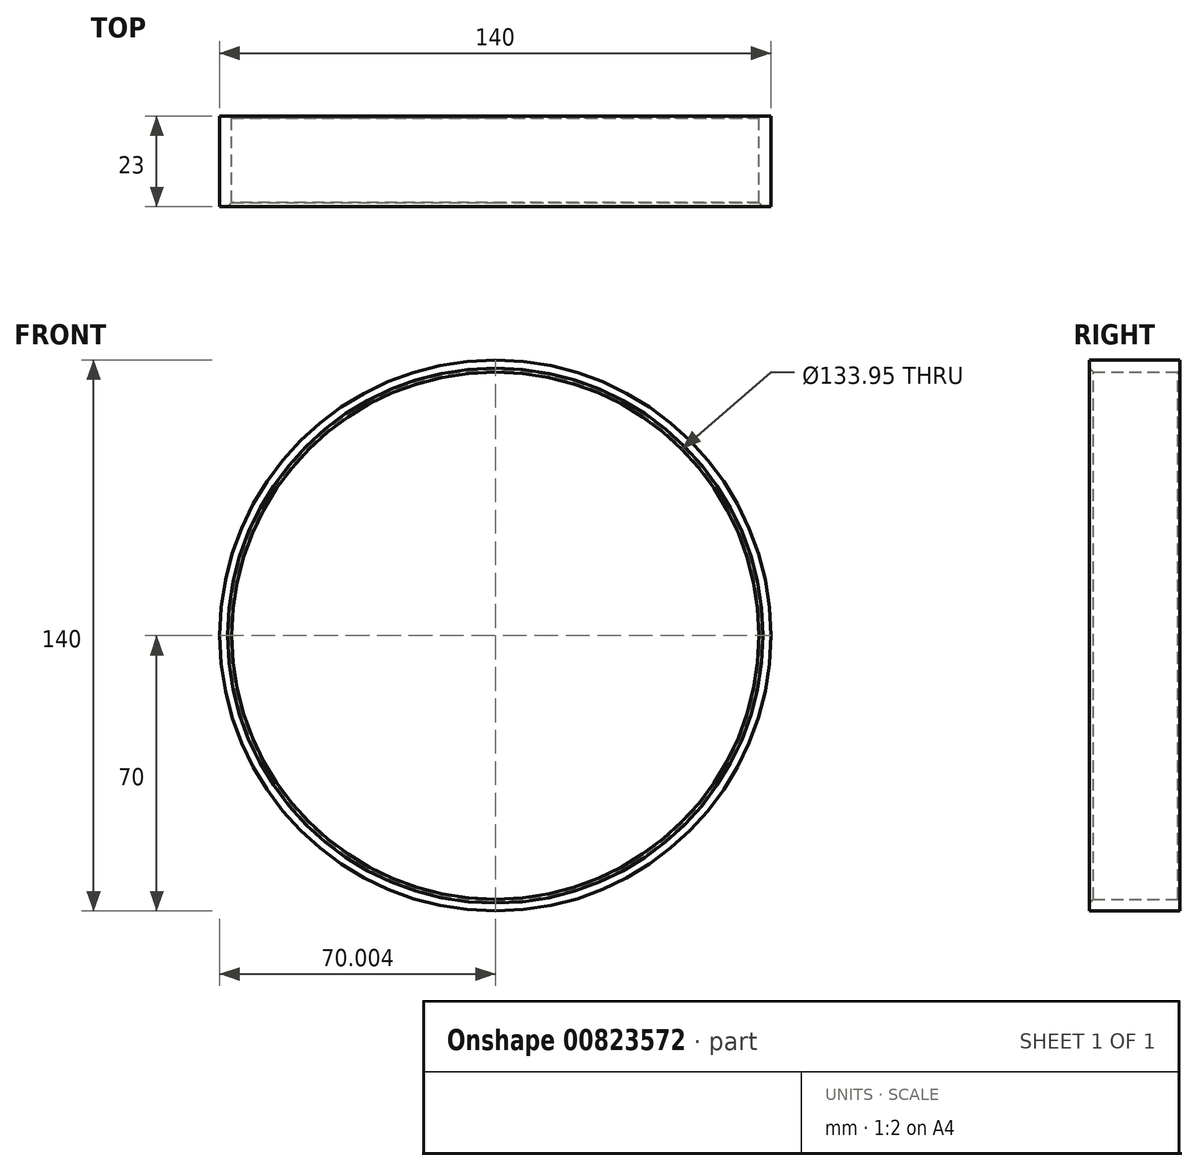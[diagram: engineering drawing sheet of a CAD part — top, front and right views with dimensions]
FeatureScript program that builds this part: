
annotation { "Feature Type Name" : "Feature", "Feature Type Description" : "" }
export const myFeature = defineFeature(function(context is Context, id is Id, definition is map)
    precondition{}
    {
        {
            var Q0;
            Q0=qCreatedBy(makeId("Front.planeOp"),FACE);
            var sketch = newSketch(context, id + "F0", { "sketchPlane" : qUnion([Q0])});
            skCircle(sketch, "E0", {"center": v(218.05, 0) * mm, "radius": 70 * mm});
            skCircle(sketch, "E1", {"center": v(218.05, 0) * mm, "radius": 66.97 * mm});
            skSolve(sketch);
        }
        {
            var Q0;
            Q0=qSketchRegion(id+"F0",true);
            extrude(context, id + "F1", {"entities" : qUnion([Q0]), "depth" : 23 * mm, "offsetDistance" : 25 * mm});
        }
        {
            var Q0;
            Q0=makeQuery(id+"F1.opExtrude","CAP_EDGE",EDGE,{"disambiguationData":[OSD([sQuery(id+"F0.wireOp",EDGE,"E1")])],"isStart":false});
            chamfer(context, id + "F2", {"entities" : qUnion([Q0]), "width" : 1 * mm, "tangentPropagation" : true});
        }
        {
            var Q0;
            Q0=makeQuery(id+"F1.opExtrude","CAP_EDGE",EDGE,{"disambiguationData":[OSD([sQuery(id+"F0.wireOp",EDGE,"E1")])],"isStart":true});
            chamfer(context, id + "F3", {"entities" : qUnion([Q0]), "width" : .5 * mm, "tangentPropagation" : true});
        }
    });
